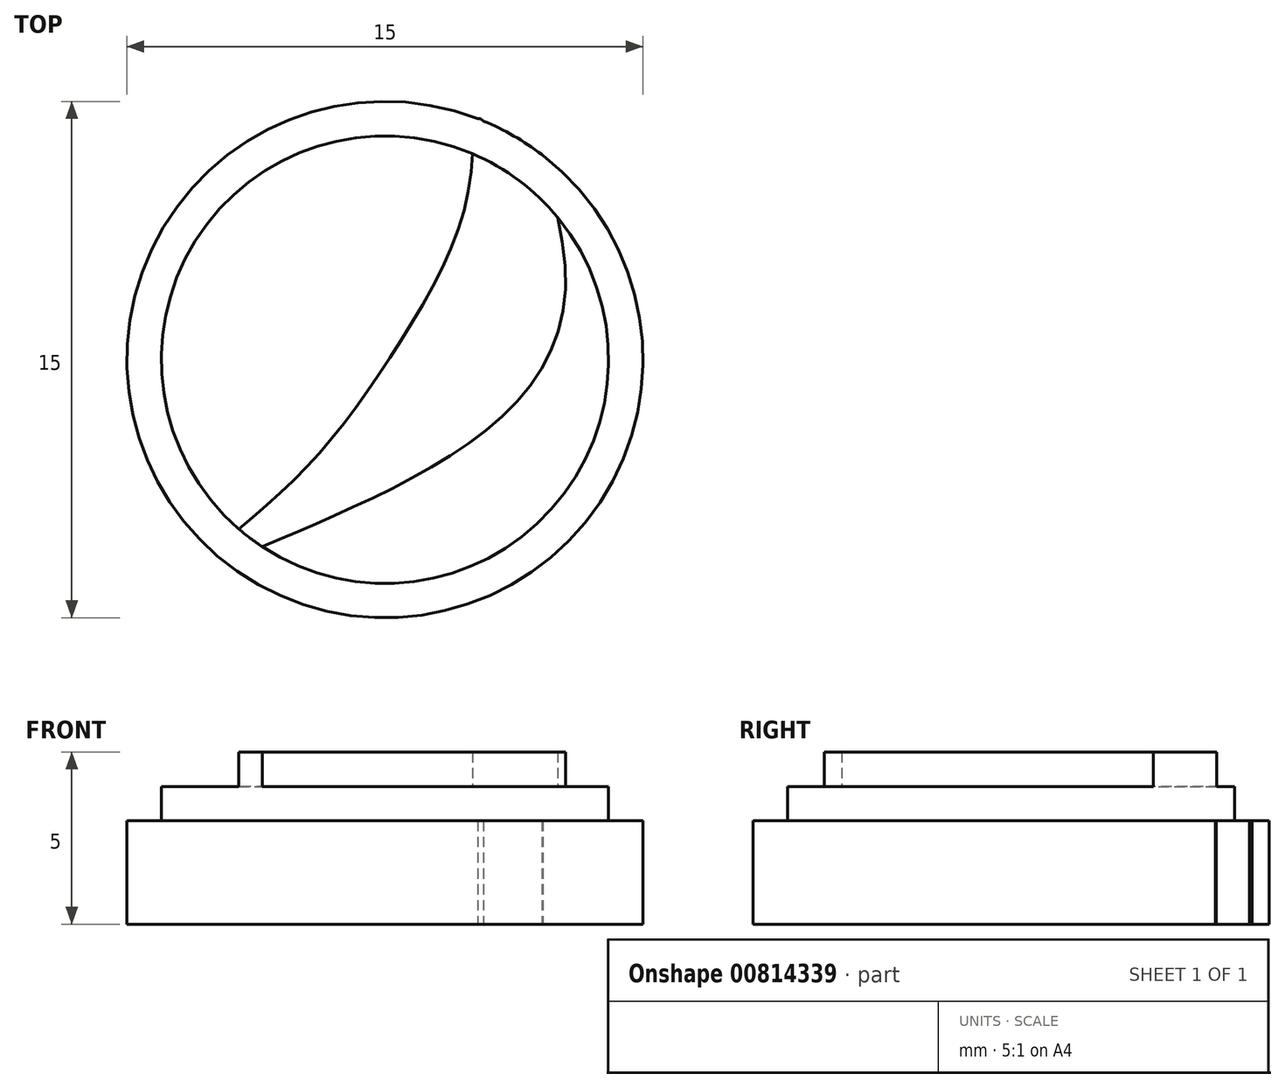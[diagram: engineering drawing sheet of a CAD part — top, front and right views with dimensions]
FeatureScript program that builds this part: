
annotation { "Feature Type Name" : "Feature", "Feature Type Description" : "" }
export const myFeature = defineFeature(function(context is Context, id is Id, definition is map)
    precondition{}
    {
        {
            var Q0;
            Q0=qCreatedBy(makeId("Top.planeOp"),FACE);
            var sketch = newSketch(context, id + "F0", { "sketchPlane" : qUnion([Q0])});
            skCircle(sketch, "E0", {"center": v(0, 0) * mm, "radius": 7.5 * mm});
            skFitSpline(sketch, "E1", {"points": [v(-5.03, -5.56) * mm, v(-2.18, -3.02) * mm, v(0.44, 0.5) * mm, v(2.41, 4.84) * mm, v(2.7, 7) * mm, v(2.87, 6.93) * mm], "startDerivative": vector(12.22, 9.9) * mm, "endDerivative": vector(3.53, -2.81) * mm});
            skFitSpline(sketch, "E2", {"points": [v(-4.65, -5.88) * mm, v(-0.85, -4.25) * mm, v(3.48, -1.58) * mm, v(5.25, 2.54) * mm, v(4.56, 5.96) * mm, v(4.6, 5.93) * mm], "startDerivative": vector(15.33, 6.28) * mm, "endDerivative": vector(1.75, -1.96) * mm});
            skCircle(sketch, "E3", {"center": v(0, 0) * mm, "radius": 6.5 * mm});
            skSolve(sketch);
        }
        {
            var Q0;
            Q0 = qSketchRegion(id + "F0", true);
            extrude(context, id + "F1", {"entities" : qUnion([Q0]), "depth" : 3 * mm, "offsetDistance" : 25 * mm});
        }
        {
            var Q0;
            {var subQ0=sQuery(id+"F0.wireOp",EDGE,"E3");var subQ1=sQuery(id+"F0.wireOp",EDGE,"E1");var subQ2=makeQuery(id+"F0.imprint","INTERSECT",VERTEX,{"disambiguationData":[OD(0.0)],"derivedFrom":[subQ1,subQ0]});Q0=makeQuery(id+"F0.imprint","IMPRINT",FACE,{"disambiguationData":[TD([[makeQuery(id+"F0.imprint","IMPRINT",EDGE,{"disambiguationData":[TD([[subQ2,-1.0]])],"derivedFrom":subQ1}),1.0]])]});}
            var Q1;
            {var subQ0=sQuery(id+"F0.wireOp",EDGE,"E3");var subQ1=sQuery(id+"F0.wireOp",EDGE,"E2");var subQ2=makeQuery(id+"F0.imprint","INTERSECT",VERTEX,{"disambiguationData":[OD(0.0)],"derivedFrom":[subQ1,subQ0]});Q1=makeQuery(id+"F0.imprint","IMPRINT",FACE,{"disambiguationData":[TD([[makeQuery(id+"F0.imprint","IMPRINT",EDGE,{"disambiguationData":[TD([[subQ2,-1.0]])],"derivedFrom":subQ1}),-1.0]])]});}
            extrude(context, id + "F2", {"entities" : qUnion([Q0, Q1]), "operationType" : NewBodyOperationType.ADD, "depth" : 4 * mm, "offsetDistance" : 25 * mm});
        }
        {
            var Q0;
            {var subQ0=sQuery(id+"F0.wireOp",EDGE,"E3");var subQ1=sQuery(id+"F0.wireOp",EDGE,"E1");var subQ2=makeQuery(id+"F0.imprint","INTERSECT",VERTEX,{"disambiguationData":[OD(0.0)],"derivedFrom":[subQ1,subQ0]});Q0=makeQuery(id+"F0.imprint","IMPRINT",FACE,{"disambiguationData":[TD([[makeQuery(id+"F0.imprint","IMPRINT",EDGE,{"disambiguationData":[TD([[subQ2,-1.0]])],"derivedFrom":subQ1}),-1.0]])]});}
            extrude(context, id + "F3", {"entities" : qUnion([Q0]), "operationType" : NewBodyOperationType.ADD, "depth" : 5 * mm, "offsetDistance" : 25 * mm});
        }
    });
